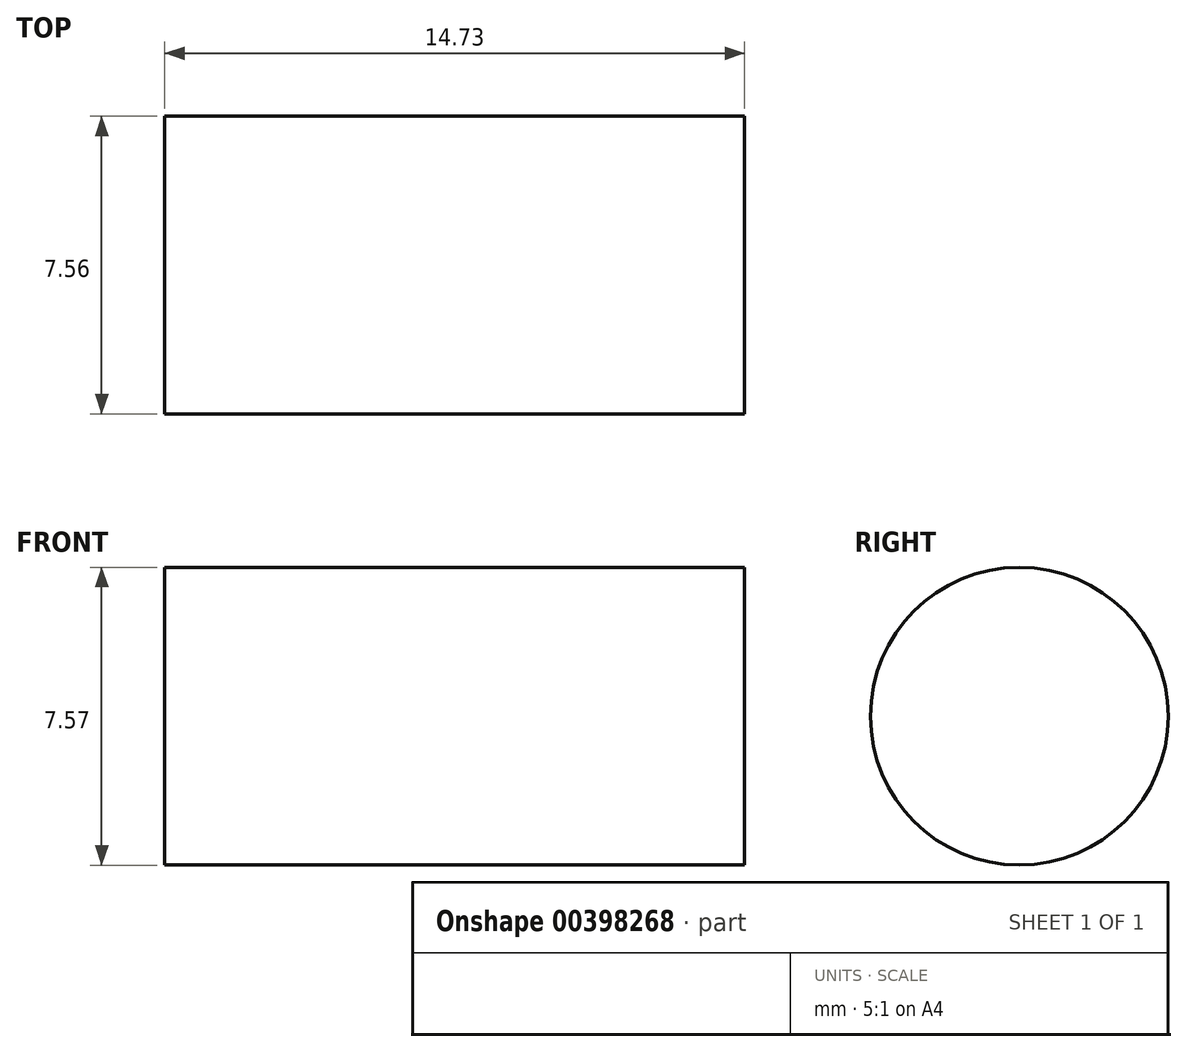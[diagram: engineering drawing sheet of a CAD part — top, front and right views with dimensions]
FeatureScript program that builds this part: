
annotation { "Feature Type Name" : "Feature", "Feature Type Description" : "" }
export const myFeature = defineFeature(function(context is Context, id is Id, definition is map)
    precondition{}
    {
        {
            var Q0;
            Q0=qCreatedBy(makeId("Front.planeOp"),FACE);
            var sketch = newSketch(context, id + "F0", { "sketchPlane" : qUnion([Q0])});
            skLineSegment(sketch, "E0", {"start": v(-12.13, 75.96) * mm, "end": v(-12.13, 0) * mm});
            skLineSegment(sketch, "E1", {"start": v(-12.13, 0) * mm, "end": v(0, 0) * mm});
            skLineSegment(sketch, "E2", {"start": v(0, 0) * mm, "end": v(12, 0) * mm});
            skLineSegment(sketch, "E3", {"start": v(12, 0) * mm, "end": v(12, 76.2) * mm});
            skLineSegment(sketch, "E4", {"start": v(12, 76.2) * mm, "end": v(-12.13, 75.96) * mm});
            skSolve(sketch);
        }
        {
            var Q0;
            {var subQ5=sQuery(id+"F0.wireOp",EDGE,"E0");Q0=makeQuery(id+"F0.imprint","IMPRINT",FACE,{"disambiguationData":[TD([[makeQuery(id+"F0.imprint","IMPRINT",EDGE,{"derivedFrom":subQ5}),1.0]])]});}
            extrude(context, id + "F1", {"entities" : qUnion([Q0]), "endBound" : BoundingType.SYMMETRIC, "depth" : 20.32 * mm});
        }
        {
            var Q0;
            Q0=qCreatedBy(makeId("Front.planeOp"),FACE);
            var sketch = newSketch(context, id + "F2", { "sketchPlane" : qUnion([Q0])});
            skLineSegment(sketch, "E5", {"start": v(0, -63.54) * mm, "end": v(2.59, -63.54) * mm});
            skLineSegment(sketch, "E6", {"start": v(2.59, -63.54) * mm, "end": v(2.59, 0) * mm});
            skLineSegment(sketch, "E7", {"start": v(0, 0) * mm, "end": v(0, -73.9) * mm, "construction": true});
            skPoint(sketch, "E8.start.orphan", {"position": v(-3.3, 0) * mm});
            skLineSegment(sketch, "E9", {"start": v(2.59, 0) * mm, "end": v(0, 0) * mm});
            skLineSegment(sketch, "E10", {"start": v(0, -63.54) * mm, "end": v(0, 0) * mm});
            skSolve(sketch);
        }
        {
            var Q0;
            Q0=makeQuery(id+"F2.imprint","IMPRINT",FACE,{"disambiguationData":[TD([[makeQuery(id+"F2.imprint","IMPRINT",EDGE,{"derivedFrom":sQuery(id+"F2.wireOp",EDGE,"E5")}),1.0]])]});
            var Q1;
            Q1=sQuery(id+"F2.wireOp",EDGE,"E7");
            revolve(context, id + "F3", {"operationType" : NewBodyOperationType.ADD, "entities" : qUnion([Q0]), "axis" : qUnion([Q1]), "revolveType" : RevolveType.FULL});
        }
        {
            var Q0;
            Q0=qCreatedBy(makeId("Right.planeOp"),FACE);
            var sketch = newSketch(context, id + "F4", { "sketchPlane" : qUnion([Q0])});
            skFitSpline(sketch, "E11", {"points": [v(0, -63.3) * mm, v(0, -70.44) * mm, v(3.06, -73.42) * mm, v(10.59, -73.9) * mm], "startDerivative": vector(-2.02, -33.47) * mm, "endDerivative": vector(22.7, 1.47) * mm});
            skSolve(sketch);
        }
        {
            var Q0;
            Q0=makeQuery(id+"F3.opRevolve","SWEPT_FACE",FACE,{"disambiguationData":[OSD([sQuery(id+"F2.wireOp",EDGE,"E5")])]});
            var Q1;
            Q1=sQuery(id+"F4.wireOp",EDGE,"E11");
            sweep(context, id + "F5", {"operationType" : NewBodyOperationType.ADD, "profiles" : qUnion([Q0]), "path" : qUnion([Q1])});
        }
        {
            var Q0;
            Q0=qCreatedBy(makeId("Top.planeOp"),FACE);
            cPlane(context, id + "F6", {"entities" : qUnion([Q0]), "cplaneType" : CPlaneType.OFFSET, "offset" : 73.15 * mm, "oppositeDirection" : true, "width" : 152.4 * mm, "height" : 152.4 * mm});
        }
        {
            var Q0;
            Q0=qCreatedBy(id+"F6.planeOp",FACE);
            var sketch = newSketch(context, id + "F7", { "sketchPlane" : qUnion([Q0])});
            skLineSegment(sketch, "E12", {"start": v(0, 10.32) * mm, "end": v(0, 24.34) * mm});
            skLineSegment(sketch, "E13", {"start": v(0, 24.34) * mm, "end": v(-6.82, 23.45) * mm});
            skLineSegment(sketch, "E14", {"start": v(-6.82, 23.45) * mm, "end": v(-6.82, 9.87) * mm});
            skLineSegment(sketch, "E15", {"start": v(-6.82, 9.87) * mm, "end": v(-14.86, 4.7) * mm});
            skLineSegment(sketch, "E16", {"start": v(-14.86, 4.7) * mm, "end": v(-16.16, 15.35) * mm});
            skLineSegment(sketch, "E17", {"start": v(-16.16, 15.35) * mm, "end": v(-26.64, 14.94) * mm});
            skLineSegment(sketch, "E18", {"start": v(-26.64, 14.94) * mm, "end": v(-18.09, 26.63) * mm});
            skLineSegment(sketch, "E19", {"start": v(-18.09, 26.63) * mm, "end": v(-25.8, 34.39) * mm});
            skLineSegment(sketch, "E20", {"start": v(-25.8, 34.39) * mm, "end": v(-16.16, 36.73) * mm});
            skLineSegment(sketch, "E21", {"start": v(-16.16, 36.73) * mm, "end": v(-13.54, 48.96) * mm});
            skLineSegment(sketch, "E22", {"start": v(-13.54, 48.96) * mm, "end": v(-6.82, 39.88) * mm});
            skLineSegment(sketch, "E23", {"start": v(-6.82, 39.88) * mm, "end": v(1, 48.96) * mm});
            skLineSegment(sketch, "E24", {"start": v(1, 48.96) * mm, "end": v(3.24, 36.73) * mm});
            skLineSegment(sketch, "E25", {"start": v(3.24, 36.73) * mm, "end": v(17.71, 39.88) * mm});
            skLineSegment(sketch, "E26", {"start": v(17.71, 39.88) * mm, "end": v(9.77, 26.87) * mm});
            skLineSegment(sketch, "E27", {"start": v(9.77, 26.87) * mm, "end": v(17.71, 23.45) * mm});
            skLineSegment(sketch, "E28", {"start": v(17.71, 23.45) * mm, "end": v(9.77, 18.39) * mm});
            skLineSegment(sketch, "E29", {"start": v(9.77, 18.39) * mm, "end": v(17.71, 13.75) * mm});
            skLineSegment(sketch, "E30", {"start": v(17.71, 13.75) * mm, "end": v(9.77, 12.53) * mm});
            skSolve(sketch);
        }
        {
            var Q0;
            Q0=makeQuery(id+"F5.opSweep","CAP_FACE",FACE,{"disambiguationData":[OSD([sQuery(id+"F2.wireOp",EDGE,"E5"),sQuery(id+"F4.wireOp",VERTEX,"E11.end")])],"isStart":false});
            var Q1;
            Q1=sQuery(id+"F7.wireOp",EDGE,"E12");
            var Q2;
            Q2=sQuery(id+"F7.wireOp",EDGE,"E13");
            var Q3;
            Q3=sQuery(id+"F7.wireOp",EDGE,"E14");
            var Q4;
            Q4=sQuery(id+"F7.wireOp",EDGE,"E15");
            var Q5;
            Q5=sQuery(id+"F7.wireOp",EDGE,"E16");
            var Q6;
            Q6=sQuery(id+"F7.wireOp",EDGE,"E17");
            var Q7;
            Q7=sQuery(id+"F7.wireOp",EDGE,"E18");
            var Q8;
            Q8=sQuery(id+"F7.wireOp",EDGE,"E19");
            var Q9;
            Q9=sQuery(id+"F7.wireOp",EDGE,"E20");
            var Q10;
            Q10=sQuery(id+"F7.wireOp",EDGE,"E21");
            var Q11;
            Q11=sQuery(id+"F7.wireOp",EDGE,"E22");
            var Q12;
            Q12=sQuery(id+"F7.wireOp",EDGE,"E23");
            var Q13;
            Q13=sQuery(id+"F7.wireOp",EDGE,"E24");
            var Q14;
            Q14=sQuery(id+"F7.wireOp",EDGE,"E25");
            var Q15;
            Q15=sQuery(id+"F7.wireOp",EDGE,"E26");
            var Q16;
            Q16=sQuery(id+"F7.wireOp",EDGE,"E27");
            var Q17;
            Q17=sQuery(id+"F7.wireOp",EDGE,"E28");
            var Q18;
            Q18=sQuery(id+"F7.wireOp",EDGE,"E29");
            var Q19;
            Q19=sQuery(id+"F7.wireOp",EDGE,"E30");
            sweep(context, id + "F8", {"operationType" : NewBodyOperationType.ADD, "profiles" : qUnion([Q0]), "path" : qUnion([Q1, Q2, Q3, Q4, Q5, Q6, Q7, Q8, Q9, Q10, Q11, Q12, Q13, Q14, Q15, Q16, Q17, Q18, Q19])});
        }
        {
            var Q0;
            Q0=makeQuery(id+"F1.opExtrude","CAP_EDGE",EDGE,{"disambiguationData":[OSD([sQuery(id+"F0.wireOp",EDGE,"E3")])],"isStart":false});
            var Q1;
            Q1=makeQuery(id+"F1.opExtrude","CAP_EDGE",EDGE,{"disambiguationData":[OSD([sQuery(id+"F0.wireOp",EDGE,"E3")])],"isStart":true});
            var Q2;
            Q2=makeQuery(id+"F1.opExtrude","CAP_EDGE",EDGE,{"disambiguationData":[OSD([sQuery(id+"F0.wireOp",EDGE,"E0")])],"isStart":true});
            var Q3;
            Q3=makeQuery(id+"F1.opExtrude","SWEPT_EDGE",EDGE,{"disambiguationData":[OSD([sQuery(id+"F0.wireOp",EDGE,"E0"),sQuery(id+"F0.wireOp",EDGE,"E1")])]});
            var Q4;
            Q4=makeQuery(id+"F1.opExtrude","CAP_EDGE",EDGE,{"disambiguationData":[OSD([sQuery(id+"F0.wireOp",EDGE,"E0")])],"isStart":false});
            var Q5;
            Q5=makeQuery(id+"F1.opExtrude","CAP_EDGE",EDGE,{"disambiguationData":[OSD([sQuery(id+"F0.wireOp",EDGE,"E1"),sQuery(id+"F0.wireOp",EDGE,"E2")])],"isStart":true});
            var Q6;
            Q6=makeQuery(id+"F1.opExtrude","SWEPT_EDGE",EDGE,{"disambiguationData":[OSD([sQuery(id+"F0.wireOp",EDGE,"E2"),sQuery(id+"F0.wireOp",EDGE,"E3")])]});
            var Q7;
            Q7=makeQuery(id+"F1.opExtrude","CAP_EDGE",EDGE,{"disambiguationData":[OSD([sQuery(id+"F0.wireOp",EDGE,"E1"),sQuery(id+"F0.wireOp",EDGE,"E2")])],"isStart":false});
            fillet(context, id + "F9", {"entities" : qUnion([Q0, Q1, Q2, Q3, Q4, Q5, Q6, Q7]), "radius" : 5.08 * mm, "tangentPropagation" : true, "allowEdgeOverflow" : false});
        }
        {
            var Q0;
            Q0=qCreatedBy(makeId("Right.planeOp"),FACE);
            var sketch = newSketch(context, id + "F10", { "sketchPlane" : qUnion([Q0])});
            skCircle(sketch, "E31", {"center": v(0, 13.12) * mm, "radius": 3.78 * mm});
            skSolve(sketch);
        }
        {
            var Q0;
            Q0=makeQuery(id+"F10.imprint","IMPRINT",FACE,{"disambiguationData":[TD([[makeQuery(id+"F10.imprint","IMPRINT",EDGE,{"derivedFrom":sQuery(id+"F10.wireOp",EDGE,"E31")}),1.0]])]});
            var Q1;
            Q1=sQuery(id+"F10.wireOp",EDGE,"E31");
            extrude(context, id + "F11", {"entities" : qUnion([Q0]), "surfaceEntities" : qUnion([Q1]), "depth" : 14.73 * mm});
        }
        {
            var Q0;
            Q0=makeQuery(id+"F1.opExtrude","CAP_EDGE",EDGE,{"disambiguationData":[OSD([sQuery(id+"F0.wireOp",EDGE,"E4")])],"isStart":false});
            var Q1;
            Q1=makeQuery(id+"F9.opFillet","BLEND_EDGE",EDGE,{"blendedFrom":[makeQuery(id+"F1.opExtrude","CAP_EDGE",EDGE,{"disambiguationData":[OSD([sQuery(id+"F0.wireOp",EDGE,"E3")])],"isStart":false}),makeQuery(id+"F1.opExtrude","SWEPT_FACE",FACE,{"disambiguationData":[OSD([sQuery(id+"F0.wireOp",EDGE,"E4")])]})],"blendedInto":[makeQuery(id+"F1.opExtrude","SWEPT_FACE",FACE,{"disambiguationData":[OSD([sQuery(id+"F0.wireOp",EDGE,"E4")])]})]});
            var Q2;
            Q2=makeQuery(id+"F1.opExtrude","SWEPT_EDGE",EDGE,{"disambiguationData":[OSD([sQuery(id+"F0.wireOp",EDGE,"E3"),sQuery(id+"F0.wireOp",EDGE,"E4")])]});
            var Q3;
            Q3=makeQuery(id+"F9.opFillet","BLEND_EDGE",EDGE,{"blendedFrom":[makeQuery(id+"F1.opExtrude","CAP_EDGE",EDGE,{"disambiguationData":[OSD([sQuery(id+"F0.wireOp",EDGE,"E3")])],"isStart":true}),makeQuery(id+"F1.opExtrude","SWEPT_FACE",FACE,{"disambiguationData":[OSD([sQuery(id+"F0.wireOp",EDGE,"E4")])]})],"blendedInto":[makeQuery(id+"F1.opExtrude","SWEPT_FACE",FACE,{"disambiguationData":[OSD([sQuery(id+"F0.wireOp",EDGE,"E4")])]})]});
            var Q4;
            Q4=makeQuery(id+"F1.opExtrude","CAP_EDGE",EDGE,{"disambiguationData":[OSD([sQuery(id+"F0.wireOp",EDGE,"E4")])],"isStart":true});
            var Q5;
            Q5=makeQuery(id+"F9.opFillet","BLEND_EDGE",EDGE,{"blendedFrom":[makeQuery(id+"F1.opExtrude","CAP_EDGE",EDGE,{"disambiguationData":[OSD([sQuery(id+"F0.wireOp",EDGE,"E0")])],"isStart":true}),makeQuery(id+"F1.opExtrude","SWEPT_FACE",FACE,{"disambiguationData":[OSD([sQuery(id+"F0.wireOp",EDGE,"E4")])]})],"blendedInto":[makeQuery(id+"F1.opExtrude","SWEPT_FACE",FACE,{"disambiguationData":[OSD([sQuery(id+"F0.wireOp",EDGE,"E4")])]})]});
            var Q6;
            Q6=makeQuery(id+"F1.opExtrude","SWEPT_EDGE",EDGE,{"disambiguationData":[OSD([sQuery(id+"F0.wireOp",EDGE,"E0"),sQuery(id+"F0.wireOp",EDGE,"E4")])]});
            var Q7;
            Q7=makeQuery(id+"F9.opFillet","BLEND_EDGE",EDGE,{"blendedFrom":[makeQuery(id+"F1.opExtrude","CAP_EDGE",EDGE,{"disambiguationData":[OSD([sQuery(id+"F0.wireOp",EDGE,"E0")])],"isStart":false}),makeQuery(id+"F1.opExtrude","SWEPT_FACE",FACE,{"disambiguationData":[OSD([sQuery(id+"F0.wireOp",EDGE,"E4")])]})],"blendedInto":[makeQuery(id+"F1.opExtrude","SWEPT_FACE",FACE,{"disambiguationData":[OSD([sQuery(id+"F0.wireOp",EDGE,"E4")])]})]});
            chamfer(context, id + "F12", {"entities" : qUnion([Q0, Q1, Q2, Q3, Q4, Q5, Q6, Q7]), "width" : 1.27 * mm, "tangentPropagation" : true});
        }
    });
